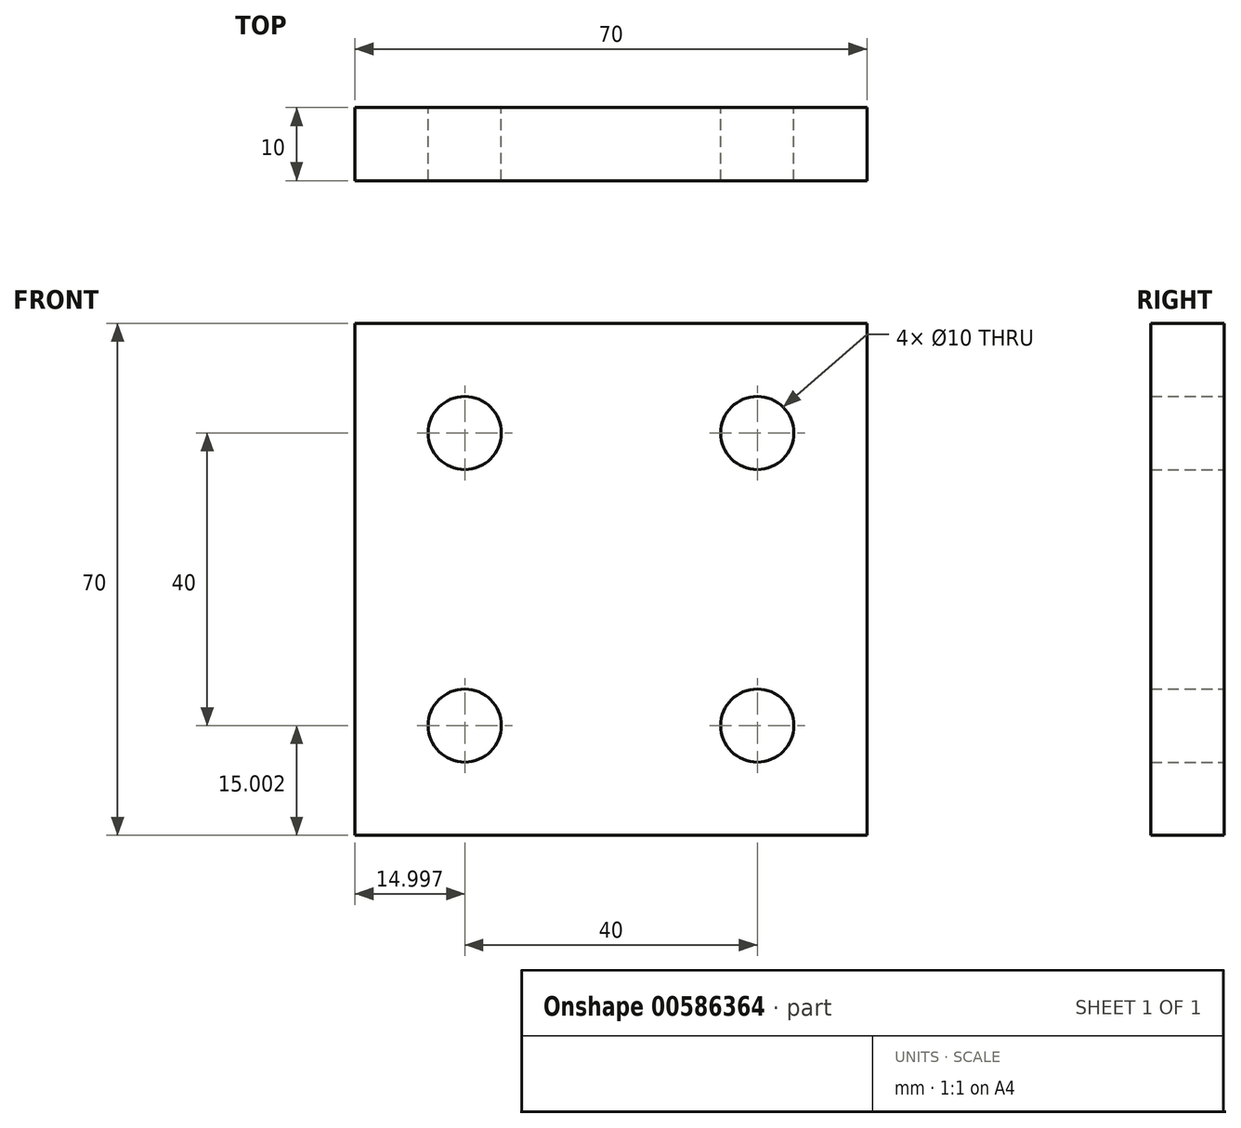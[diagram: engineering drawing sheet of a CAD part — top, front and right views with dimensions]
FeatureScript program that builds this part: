
annotation { "Feature Type Name" : "Feature", "Feature Type Description" : "" }
export const myFeature = defineFeature(function(context is Context, id is Id, definition is map)
    precondition{}
    {
        {
            var Q0;
            Q0=qCreatedBy(makeId("Front.planeOp"),FACE);
            var sketch = newSketch(context, id + "F0", { "sketchPlane" : qUnion([Q0])});
            skLineSegment(sketch, "E0.bottom", {"start": v(35.19, 37.25) * mm, "end": v(-34.81, 37.25) * mm});
            skLineSegment(sketch, "E0.top", {"start": v(35.19, -32.75) * mm, "end": v(-34.81, -32.75) * mm});
            skLineSegment(sketch, "E0.left", {"start": v(35.19, 37.25) * mm, "end": v(35.19, -32.75) * mm});
            skLineSegment(sketch, "E0.right", {"start": v(-34.81, 37.25) * mm, "end": v(-34.81, -32.75) * mm});
            skCircle(sketch, "E1", {"center": v(-19.81, 22.25) * mm, "radius": 5 * mm});
            skCircle(sketch, "E2", {"center": v(20.19, 22.25) * mm, "radius": 5 * mm});
            skCircle(sketch, "E3", {"center": v(-19.81, -17.75) * mm, "radius": 5 * mm});
            skCircle(sketch, "E4", {"center": v(20.19, -17.75) * mm, "radius": 5 * mm});
            skSolve(sketch);
        }
        {
            var Q0;
            Q0=makeQuery(id+"F0.imprint","IMPRINT",FACE,{"disambiguationData":[TD([[makeQuery(id+"F0.imprint","IMPRINT",EDGE,{"derivedFrom":sQuery(id+"F0.wireOp",EDGE,"E0.bottom")}),1.0]])]});
            extrude(context, id + "F1", {"entities" : qUnion([Q0]), "depth" : 10 * mm, "offsetDistance" : 25 * mm});
        }
    });
